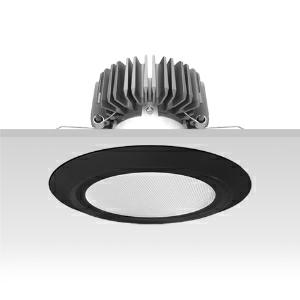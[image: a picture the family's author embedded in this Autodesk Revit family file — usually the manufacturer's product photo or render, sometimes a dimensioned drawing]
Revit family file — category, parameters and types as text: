
# Revit family: 3f_filippi_-_3f_reno_bianco_ampio_3f_filippi_-_30625_a01038_-_3f_reno_200_wh_2000-930_wide___vs_bk_39f7
name_source: partatom
category: Lighting Fixtures
units: mm (PartAtom-declared; Revit-internal decimal feet)

## family parameters
Cut with Voids When Loaded = No
Host = Face
Light Source = No
Part Type = Normal
Room Calculation Point = No
Round Connector Dimension = Use Diameter
Shared = No

## types (1)
- 3F Filippi - 3F Reno Bianco Ampio (1 x LED, 1650 lm, 24 W, 3000 K)
    Apparent Load = 24 VA
    Approval mark = CE
    CIE Flux Codes = 75 94 99 100 100
    Color Rendering = 90
    Color Temperature = 3000 K
    Control Gear = Electronic ballast
    Default Elevation = 1800 mm
    Description = ILLUMINOTECHNICAL
Luminous efficiency 100% (DLOR 100%, ULOR 0%).
Initial luminous flux of the luminaire 1650 lm.
Direct symmetric wide distribution.
Installation Interdistance Transv.D = 1.16 x hu - Long.D = 1.14 x hu.
Average luminance <3000 cd/m² for radial angles >65°.
Tabular UGR (CIE 117 - 4H-8H; S=0.25H; 70/50/20): RUG 20.3 - 20.2.
Beam angle: 74° - 74°.
Luminous efficacy 69 lm/W.
Lifetime (L90/B10): 30000 h. (tq+25°C)
Lifetime (L85/B10): 50000 h. (tq+25°C)
Lifetime (L70/B10): 80000 h. (tq+25°C)
Sudden decreased luminous flux after 50000 hours: 0% (C0).
Photobiological safety in compliance with IEC/TR 62778: RG0 risk exempt, (IEC 62471).
In compliance with IEC/EN 62722-2-1 - IEC/EN 62717 standards.

SOURCE
Compact LED module 2000/930.
Energy efficiency class (UE 2019/2020 - UE 2019/2015): E.
CIE 13.3 Colour rendering index: CRI >90 (R9 >50%).
IES TM-30 Fidelity Index: Rf = 92 Rg = 101.
CCT nominal colour temperature 3000 K.
Colour initial tolerance (MacAdam): SDCM 3.
Zhaga Book 3 compliant.

MECHANICAL
Passive heat dissipator in die-casting aluminium, oversized, for optimum thermal management of the LED module.
Parabolic element with graduated/concentric rings in white polycarbonate.
Transparent external lens with glossy and satin differentiated surfaces, with a cooling and anti-insect system in methacrylate (PMMA).
Fastening spring clips in stainless steel.
Dimensions: diameter 226 mm, height 146 mm. Weight 1.14 kg.
IP44 protection degree for exposed part, IP20 for recessed part.
Mechanical strength to impacts IK06 (1 joule).
Glow-wire test resistance 650°C.

ELECTRICAL
Wiring on a separate unit.
Halogen Free electronic wiring 230V-50/60Hz, power factor 0.95, THD <25%, constant output current, SELV, class II, 1 driver.
Power of the luminaire 24 W.
ENEC - CE.
SAFE FLICKER: PstLM=<1 and SVM=<0.4 (IEC TR 61547-1 and IEC TR 63158), to ensure a more comfortable and safe light.
Luminaire compliant with EN 60598-2-22 for power supply from a centralised emergency system CPSS (Central Power Supply System), not incorporated in the luminaire - high risk areas excluded. The default power and flux are 100% in AC and 100% in DC.
Ambient temperature from 0°C to +25°C.
Temperature class T6 max 85°C.
Relative humidity UR: <85%.

INSTALLATION
Pull-up recessed fitting.
False ceiling carving: 200 mm.
All accessories dedicated to this product are available on the Catalog and on our website www.3F-Filippi.com.

ACCESSORIES
A01038 - Anti-glare microprismatic VS moulded glass, tempered, not flammable, locked and in line with the trim, in black polycarbonate.

APPLICATIONS
Environments: architectural, commercial, exhibition areas, transit areas, corridors, shops, display windows, service areas.
In false ceilings with narrow voids.

WARNING
Luminaire designed for disposal/recycling at end-of-life.
Replaceable (LED only) light source by a professional. Replaceable control gear by a professional.
    Height = 0 mm  [stored 0 ft]
    Lamp = 1 x LED
    Lamp Light Flux = 1650 lm
    Lamp Power = 24 W
    Lamp count = 1
    Length = 226 mm
    Lifetime = 50000 h
    Luminous efficacy = 69 lm/W
    Manufacturer = 3F Filippi
    ModVariant = No
    Model = 3F Filippi - 30625+A01038 - 3F Reno 200 WH 2000-930 WIDE + VS BK
    Mounting Place = Ceiling
    Mounting Type = Recessed
    Number of Poles = 1
    OnlyDefault = Yes
    Power Factor = 1
    Product Name = 3F Filippi - 3F Reno Bianco Ampio
    Product group = recessed luminaire
    ProductGroupID = 4
    Protection Class = Protection class II
    Protection Degree = IP 20
    RLX_Detail_Level = 1
    RLX_Emergency_Light_Flux = 0 lm
    RLX_Emergency_Type = 0
    RLX_Emergency_Type_DB = No
    RlxData = <blob elided: 97405 chars, md5=99b1cc10>
    Socket = socket
    Standby Power = 0 W
    System Light Flux = 1650 lm
    System Power = 24 W
    Type Comments = Product without accessories
    Type Image = 3ffilippi_3f_reno_200_bk_vs_smp.jpg
    URL = http://relux.com
    VarID = ---
    Voltage = 0 V
    Weight = 0.00 kg
    Width = 0 mm  [stored 0 ft]

note: [stored X ft] marks values corroborated as IEEE doubles in the binary element streams (Revit-internal decimal feet)

## geometry (parser evidence)
native form markers: Blend x4, Sweep x11
no freeform markers — native parametric forms only
